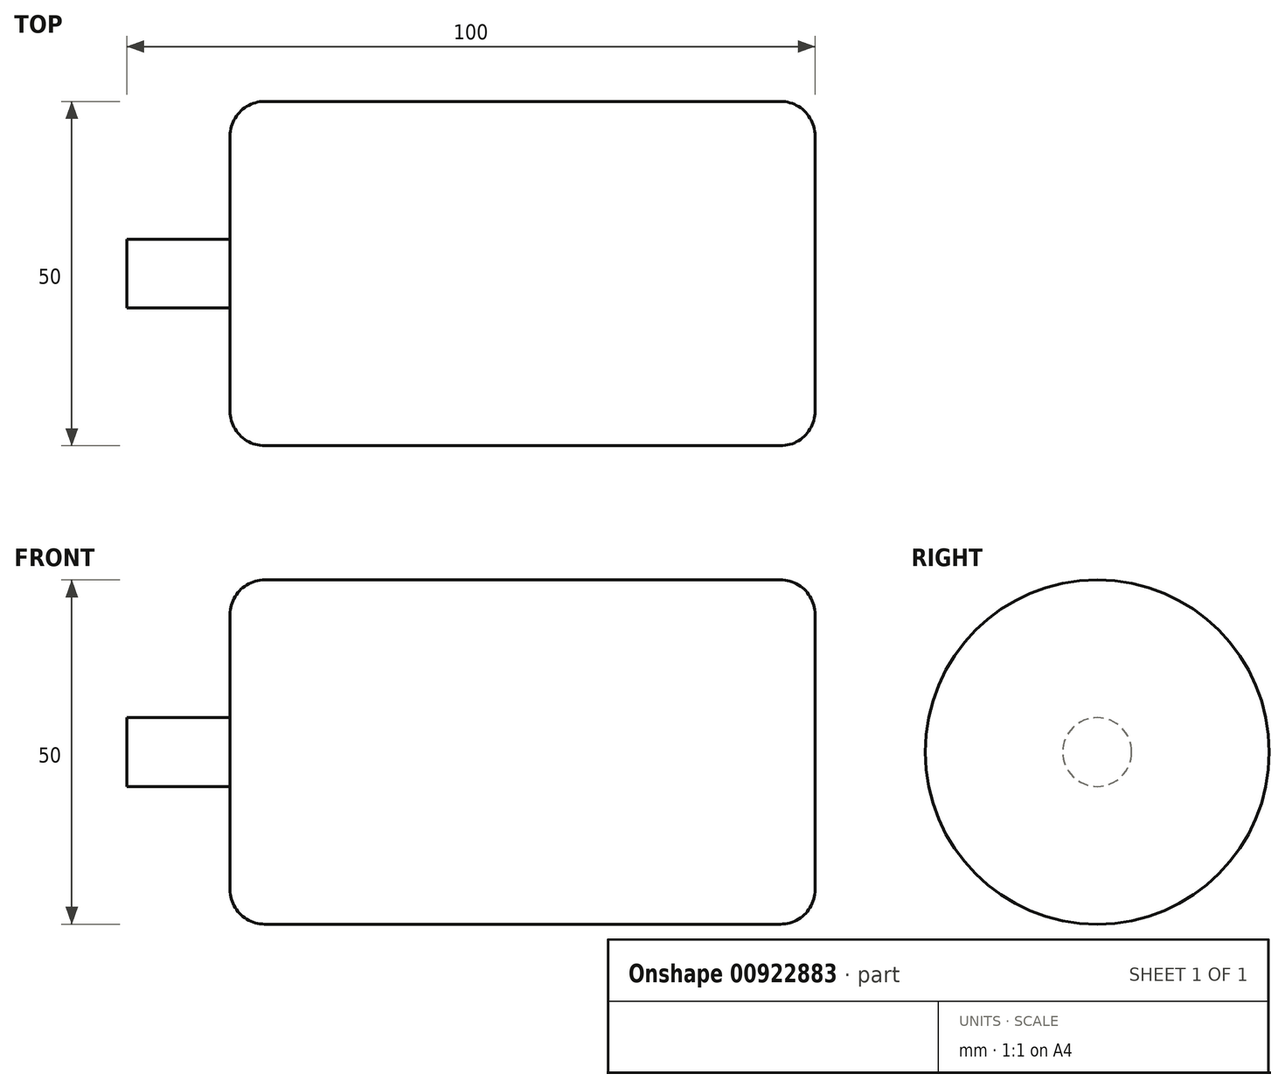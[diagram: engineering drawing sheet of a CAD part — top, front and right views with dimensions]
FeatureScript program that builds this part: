
annotation { "Feature Type Name" : "Feature", "Feature Type Description" : "" }
export const myFeature = defineFeature(function(context is Context, id is Id, definition is map)
    precondition{}
    {
        {
            var Q0;
            Q0=qCreatedBy(makeId("Top.planeOp"),FACE);
            var sketch = newSketch(context, id + "F0", { "sketchPlane" : qUnion([Q0])});
            skLineSegment(sketch, "E0", {"start": v(0, 0) * mm, "end": v(0, 5) * mm});
            skLineSegment(sketch, "E1", {"start": v(0, 5) * mm, "end": v(15, 5) * mm});
            skLineSegment(sketch, "E2", {"start": v(15, 5) * mm, "end": v(15, 25) * mm});
            skLineSegment(sketch, "E3", {"start": v(15, 25) * mm, "end": v(100, 25) * mm});
            skLineSegment(sketch, "E4", {"start": v(100, 25) * mm, "end": v(100, 0) * mm});
            skLineSegment(sketch, "E5", {"start": v(100, 0) * mm, "end": v(0, 0) * mm});
            skSolve(sketch);
        }
        {
            var Q0;
            Q0 = qSketchRegion(id + "F0", true);
            var Q1;
            Q1=sQuery(id+"F0.wireOp",EDGE,"E5");
            revolve(context, id + "F1", {"surfaceOperationType" : NewSurfaceOperationType.NEW, "entities" : qUnion([Q0]), "axis" : qUnion([Q1]), "revolveType" : RevolveType.FULL});
        }
        {
            var Q0;
            Q0=makeQuery(id+"F1.opRevolve","SWEPT_EDGE",EDGE,{"disambiguationData":[OSD([sQuery(id+"F0.wireOp",EDGE,"E2"),sQuery(id+"F0.wireOp",EDGE,"E3")])]});
            var Q1;
            Q1=makeQuery(id+"F1.opRevolve","SWEPT_EDGE",EDGE,{"disambiguationData":[OSD([sQuery(id+"F0.wireOp",EDGE,"E3"),sQuery(id+"F0.wireOp",EDGE,"E4")])]});
            fillet(context, id + "F2", {"entities" : qUnion([Q0, Q1]), "radius" : 5 * mm, "tangentPropagation" : true, "allowEdgeOverflow" : false});
        }
    });
